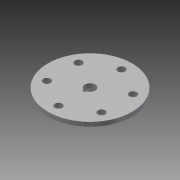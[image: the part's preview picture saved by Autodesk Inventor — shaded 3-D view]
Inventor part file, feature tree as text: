
AUTODESK INVENTOR PART (.ipt)
format: ipt  version: 2013 (Build 170138000, 138)  size: 120,320 bytes
history: native  units: in
note: dims shown in document units (in); Inventor stores cm internally (conversion verified against a paired STEP export)
features: extrude x3, sketch x3
ambient origin geometry x8: Origin, YZ Plane, XZ Plane, XY Plane, X Axis, Y Axis, Z Axis, Center Point
feature tree (6):
  extrude  "Extrusion3"  Depth=0.22in
  extrude  "Extrusion4"  Depth=0.375in
  extrude  "Extrusion5"  Depth=0.9375in
  sketch  "Sketch1"  dims[d0=0.375in d5=0.22in]
  sketch  "Sketch3"  dims[d7=2.3622in d9=360.0deg d22=0.375in]
  sketch  "Sketch4"  dims[d23=0.125in d24=0.0in d25=0.9375in d26=0.315in d27=0.125in d28=0.0in d29=0.0394in d30=0.0394in d31=0.1969in d32=0.125in d33=0.0in]
